# Revit family: Digital_Media-Honeywell-VARIODYN_D1-583381-31
name_source: partatom
category: Electrical Equipment
revit_build: Autodesk Revit 2017 (Build: 20160225_1515(x64)
units: mm (PartAtom-declared; Revit-internal decimal feet)

## family parameters
Cut with Voids When Loaded = No
Host = Face
OmniClass Number = 23.85.50.00
OmniClass Title = Communication Systems
Part Type = Equipment Switch
Room Calculation Point = No
Round Connector Dimension = Use Diameter
Shared = No

## types (1)
- System Communication Unit SCU - 583381.31
    Air Humidity = 15 ... 90 %
    Ambient Temperature = -5 °C ... 45 °C
    Apparent Load = 0 VA
    Default Elevation = 1219 mm
    Depth = 360 mm  [stored 1.1811 ft]
    Description = System Communication Unit SCU
    Finish = Metal - Honeywell - Stainless Steel - Black
    Frequency = 47 Hz
    Height = 44 mm  [stored 0.144357 ft]
    Load Sub-Classification = No
    Manufacturer = Honeywell International
    Manufacturer Fax Number = 02131/40615-606
    Model = 583381.31
    Number of Poles = 1
    Power Consumption = 24 W
    Power Factor = 1
    Product Documentation Link = https://www.esser-systems.com
    Product Name = SCU
    Product Page URL = https://www.esser-systems.com
    Rated Frequency = 47 ... 63 Hz
    Rated Voltage = 90 ... 265 V AC
    URL = www.esser-systems.com
    Utility = No
    Version = 2017 - v1.0a
    Voltage = 90 V
    Wattage = 24 W
    Watts = 24 W
    Weight = 3.00 kgf
    Width = 483 mm

note: [stored X ft] marks values corroborated as IEEE doubles in the binary element streams (Revit-internal decimal feet)

## geometry (parser evidence)
native form markers: Sweep x1
no freeform markers — native parametric forms only
